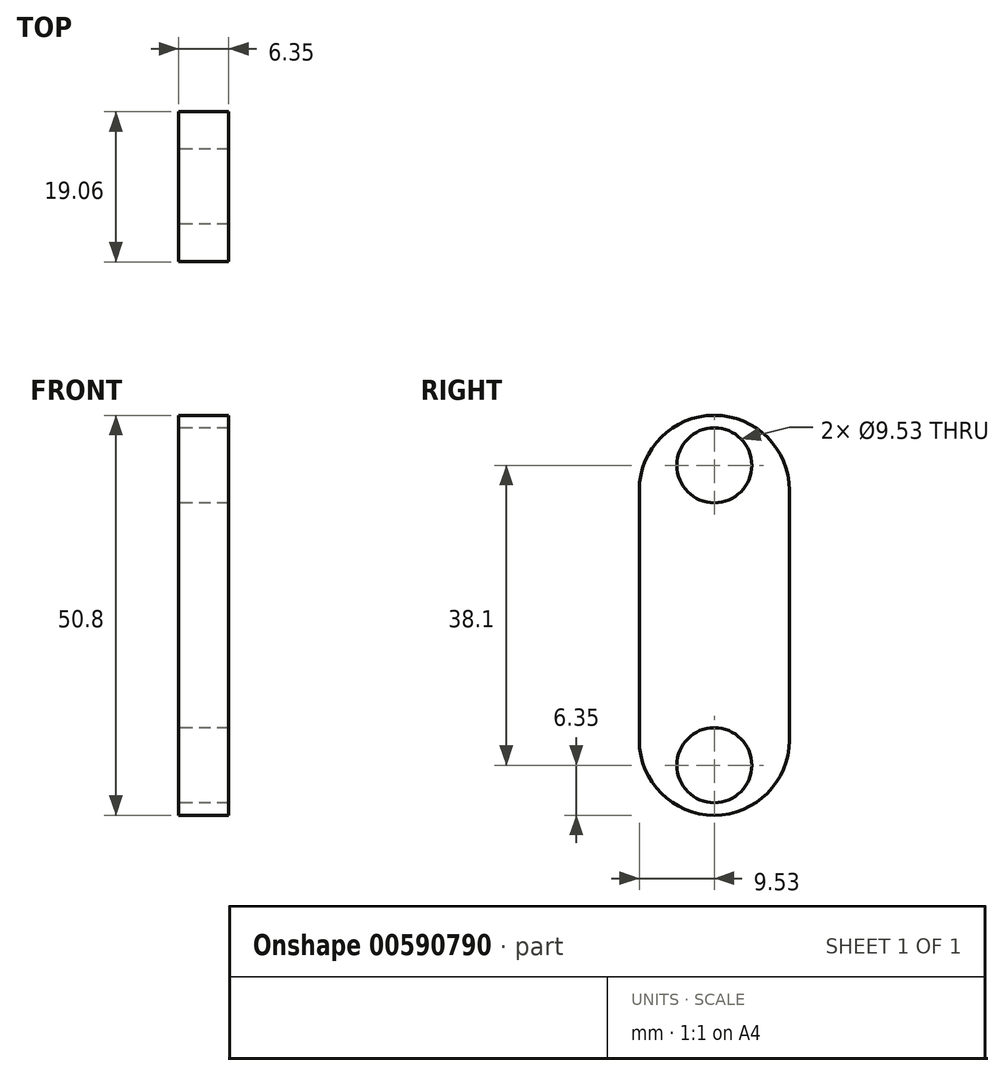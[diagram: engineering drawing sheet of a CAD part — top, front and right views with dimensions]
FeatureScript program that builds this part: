
annotation { "Feature Type Name" : "Feature", "Feature Type Description" : "" }
export const myFeature = defineFeature(function(context is Context, id is Id, definition is map)
    precondition{}
    {
        {
            var Q0;
            Q0=qCreatedBy(makeId("Right.planeOp"),FACE);
            var sketch = newSketch(context, id + "F0", { "sketchPlane" : qUnion([Q0])});
            skLineSegment(sketch, "E0.bottom", {"start": v(9.53, 25.4) * mm, "end": v(-9.53, 25.4) * mm});
            skLineSegment(sketch, "E0.top", {"start": v(9.52, -25.4) * mm, "end": v(-9.53, -25.4) * mm});
            skLineSegment(sketch, "E0.left", {"start": v(9.53, 25.4) * mm, "end": v(9.52, -25.4) * mm});
            skLineSegment(sketch, "E0.right", {"start": v(-9.53, 25.4) * mm, "end": v(-9.53, -25.4) * mm});
            skPoint(sketch, "E0.middle", {"position": v(0, 0) * mm});
            skCircle(sketch, "E1", {"center": v(0, 19.05) * mm, "radius": 4.76 * mm});
            skCircle(sketch, "E2", {"center": v(0, -19.05) * mm, "radius": 4.76 * mm});
            skSolve(sketch);
        }
        {
            var Q0;
            Q0 = qSketchRegion(id + "F0", true);
            extrude(context, id + "F1", {"entities" : qUnion([Q0]), "depth" : 6.35 * mm, "offsetDistance" : 25.4 * mm});
        }
        {
            var Q0;
            Q0=makeQuery(id+"F1.opExtrude","SWEPT_EDGE",EDGE,{"disambiguationData":[OSD([sQuery(id+"F0.wireOp",EDGE,"E0.bottom"),sQuery(id+"F0.wireOp",EDGE,"E0.left")])]});
            var Q1;
            Q1=makeQuery(id+"F1.opExtrude","SWEPT_EDGE",EDGE,{"disambiguationData":[OSD([sQuery(id+"F0.wireOp",EDGE,"E0.bottom"),sQuery(id+"F0.wireOp",EDGE,"E0.right")])]});
            var Q2;
            Q2=makeQuery(id+"F1.opExtrude","SWEPT_EDGE",EDGE,{"disambiguationData":[OSD([sQuery(id+"F0.wireOp",EDGE,"E0.top"),sQuery(id+"F0.wireOp",EDGE,"E0.left")])]});
            var Q3;
            Q3=makeQuery(id+"F1.opExtrude","SWEPT_EDGE",EDGE,{"disambiguationData":[OSD([sQuery(id+"F0.wireOp",EDGE,"E0.top"),sQuery(id+"F0.wireOp",EDGE,"E0.right")])]});
            fillet(context, id + "F2", {"entities" : qUnion([Q0, Q1, Q2, Q3]), "tangentPropagation" : true, "radius" : 9.52 * mm, "defaultsChanged" : false, "vertexSettings" : [], "allowEdgeOverflow" : false});
        }
    });
